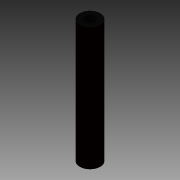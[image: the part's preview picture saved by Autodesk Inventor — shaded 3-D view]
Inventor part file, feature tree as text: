
AUTODESK INVENTOR PART (.ipt)
format: ipt  version: 2013 (Build 170138000, 138)  size: 82,944 bytes
history: native  units: in
note: dims shown in document units (in); Inventor stores cm internally (conversion verified against a paired STEP export)
features: extrude x1, sketch x1
ambient origin geometry x8: Origin, YZ Plane, XZ Plane, XY Plane, X Axis, Y Axis, Z Axis, Center Point
bodies: Solid1 (feature_tree)
feature tree (2):
  extrude  "Extrusion1"  Depth=0.25in
  sketch  "Sketch1"  dims[d0=0.5in d1=0.25in d2=3.0in d3=0.0in]
